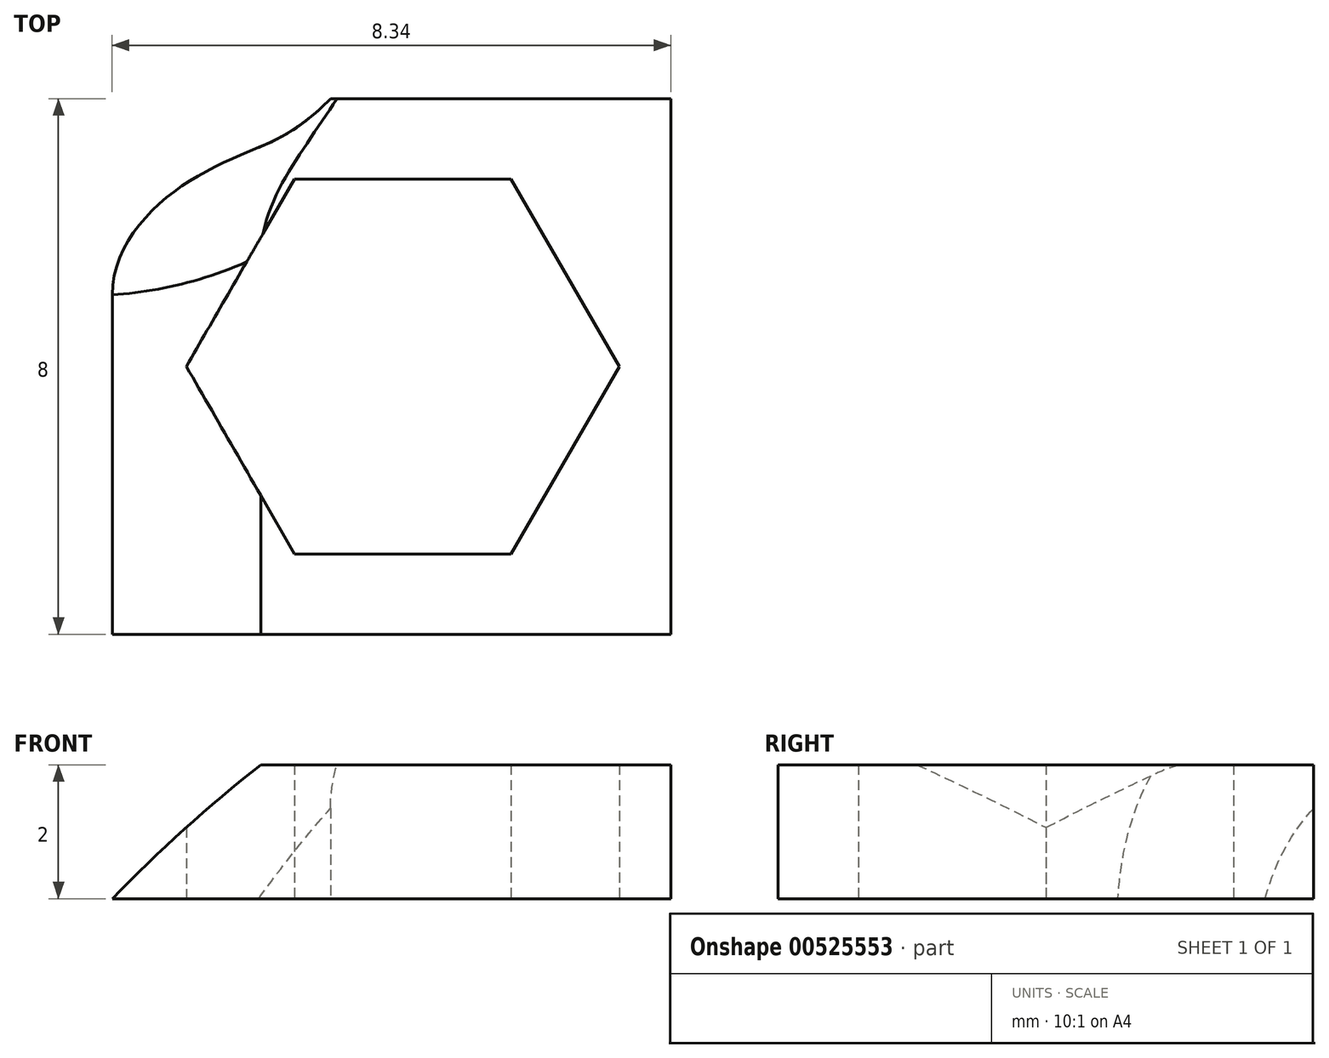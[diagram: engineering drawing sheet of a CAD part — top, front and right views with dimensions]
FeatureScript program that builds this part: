
annotation { "Feature Type Name" : "Feature", "Feature Type Description" : "" }
export const myFeature = defineFeature(function(context is Context, id is Id, definition is map)
    precondition{}
    {
        {
            var Q0;
            Q0=qCreatedBy(makeId("Top.planeOp"),FACE);
            var sketch = newSketch(context, id + "F0", { "sketchPlane" : qUnion([Q0])});
            skLineSegment(sketch, "E0", {"start": v(4, 4) * mm, "end": v(-4.34, 4) * mm});
            skLineSegment(sketch, "E1", {"start": v(4, 4) * mm, "end": v(4, -4) * mm});
            skLineSegment(sketch, "E2", {"start": v(4, -4) * mm, "end": v(-4.34, -4) * mm});
            skLineSegment(sketch, "E3", {"start": v(-4.34, -4) * mm, "end": v(-4.34, 4) * mm});
            skCircle(sketch, "E4.6", {"center": v(0, 0) * mm, "radius": 1.5 * mm});
            skCircle(sketch, "E5.cCircle", {"center": v(0, 0) * mm, "radius": 2.8 * mm, "construction": true});
            skLineSegment(sketch, "E5.0", {"start": v(1.62, 2.8) * mm, "end": v(3.23, 0) * mm});
            skLineSegment(sketch, "E5.1", {"start": v(3.23, 0) * mm, "end": v(1.62, -2.8) * mm});
            skLineSegment(sketch, "E5.2", {"start": v(1.62, -2.8) * mm, "end": v(-1.62, -2.8) * mm});
            skLineSegment(sketch, "E5.3", {"start": v(-1.62, -2.8) * mm, "end": v(-3.23, 0) * mm});
            skLineSegment(sketch, "E5.4", {"start": v(-3.23, 0) * mm, "end": v(-1.62, 2.8) * mm});
            skLineSegment(sketch, "E5.5", {"start": v(-1.62, 2.8) * mm, "end": v(1.62, 2.8) * mm});
            skSolve(sketch);
        }
        {
            var Q0;
            Q0=makeQuery(id+"F0.imprint","IMPRINT",FACE,{"disambiguationData":[TD([[makeQuery(id+"F0.imprint","IMPRINT",EDGE,{"derivedFrom":sQuery(id+"F0.wireOp",EDGE,"E0")}),1.0]])]});
            extrude(context, id + "F1", {"entities" : qUnion([Q0]), "depth" : 2 * mm, "offsetDistance" : 25 * mm});
        }
        {
            var Q0;
            Q0=qCreatedBy(makeId("Front.planeOp"),FACE);
            var sketch = newSketch(context, id + "F2", { "sketchPlane" : qUnion([Q0])});
            skArc(sketch, "E6.0", {"start": v(-1.02, 2.82) * mm, "mid": v(-2.75, 1.49) * mm, "end": v(-4.34, 0) * mm});
            skLineSegment(sketch, "E7", {"start": v(-1.02, 2.82) * mm, "end": v(-10.56, 2.82) * mm});
            skLineSegment(sketch, "E8", {"start": v(-10.56, 2.82) * mm, "end": v(-10.56, 0) * mm});
            skLineSegment(sketch, "E9", {"start": v(-10.56, 0) * mm, "end": v(-4.34, 0) * mm});
            skSolve(sketch);
        }
        {
            var Q0;
            Q0 = qSketchRegion(id + "F2", true);
            extrude(context, id + "F3", {"entities" : qUnion([Q0]), "operationType" : NewBodyOperationType.REMOVE, "endBound" : BoundingType.SYMMETRIC, "depth" : 25 * mm, "offsetDistance" : 25 * mm});
        }
        {
            var Q0;
            Q0=qCreatedBy(makeId("Top.planeOp"),FACE);
            var sketch = newSketch(context, id + "F4", { "sketchPlane" : qUnion([Q0])});
            skCircle(sketch, "E10", {"center": v(-3.26, 6.06) * mm, "radius": 3 * mm});
            skCircle(sketch, "E11.MirrorC", {"center": v(-3.26, -6.06) * mm, "radius": 3 * mm});
            skSolve(sketch);
        }
        {
            var Q0;
            Q0=makeQuery(id+"F4.imprint","IMPRINT",FACE,{"disambiguationData":[TD([[makeQuery(id+"F4.imprint","IMPRINT",EDGE,{"derivedFrom":sQuery(id+"F4.wireOp",EDGE,"E10")}),1.0]])]});
            extrude(context, id + "F5", {"entities" : qUnion([Q0]), "operationType" : NewBodyOperationType.REMOVE, "endBound" : BoundingType.SYMMETRIC, "depth" : 25 * mm, "offsetDistance" : 25 * mm});
        }
        {
            var Q0;
            Q0=makeQuery(id+"F1.opExtrude","CAP_EDGE",EDGE,{"disambiguationData":[OSD([sQuery(id+"F0.wireOp",EDGE,"d3942829-5e7f-476c-ad5e-3b37c4d40019.0")])],"isStart":false});
            var Q1;
            Q1=makeQuery(id+"F5.boolean.opBoolean","INTERSECT",EDGE,{"derivedFrom":[makeQuery(id+"F3.boolean.opBoolean","COPY",FACE,{"derivedFrom":makeQuery(id+"F3.opExtrude","SWEPT_FACE",FACE,{"disambiguationData":[OSD([sQuery(id+"F2.wireOp",EDGE,"E6.0")])]})}),makeQuery(id+"F5.opExtrude","SWEPT_FACE",FACE,{"disambiguationData":[OSD([sQuery(id+"F4.wireOp",EDGE,"E10")])]})]});
            fillet(context, id + "F6", {"entities" : qUnion([Q0, Q1]), "radius" : 2 * mm, "tangentPropagation" : true, "allowEdgeOverflow" : false});
        }
    });
